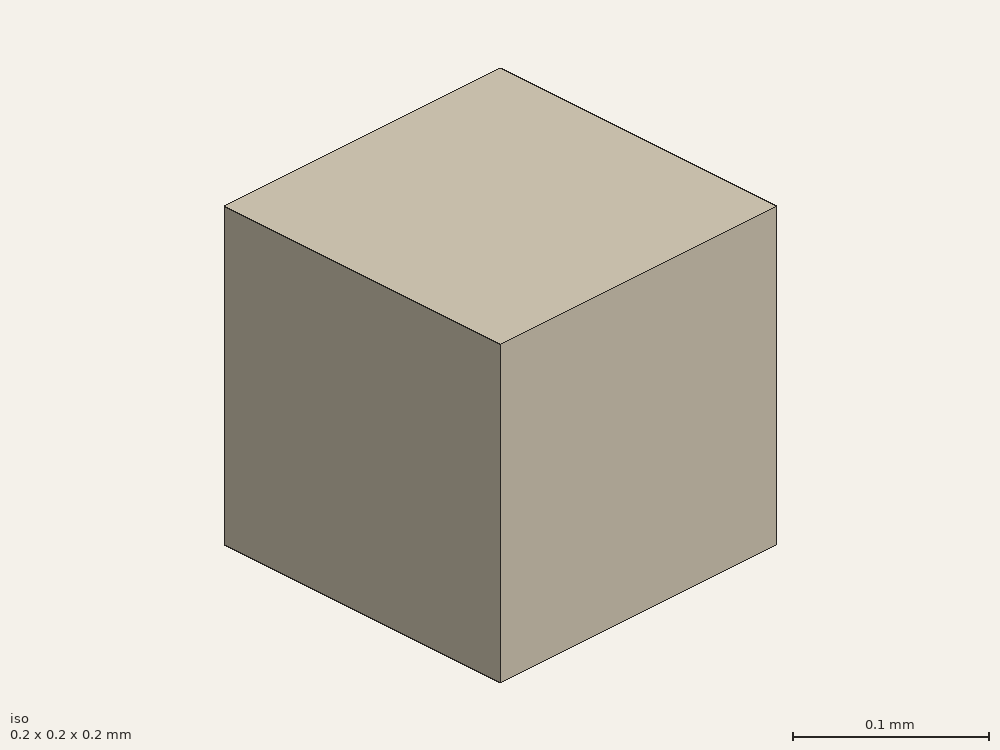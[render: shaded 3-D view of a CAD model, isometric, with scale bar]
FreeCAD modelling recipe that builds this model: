
FCSTD DOCUMENT  (FreeCAD 0.21R33694 (Git))
Label: monopole_antenna
License: All rights reserved
LicenseURL: http://en.wikipedia.org/wiki/All_rights_reserved
objects: Part::Part2DObjectPython×14, App::FeaturePython×8, Part::Extrusion×6, Part::Cut×5, Part::FeaturePython×2
note: 27 computed .brp shape members not serialized (recipe doc carries the construction recipe); baked Part::Feature solids carry a one-line shape summary decoded from their .brp

FEATURE [Part::Part2DObjectPython] Polygon  # Draft 2D object (typed FeaturePython)
  Area = 1.08e-06
  ChamferSize = 0
  DrawMode = 0
  FacesNumber = 12
  FilletRadius = 0
  MakeFace = true
  Radius = 0.0006
FEATURE [Part::Extrusion] Extrude  label="pin"
  Base = -> Polygon
  Dir = (0,0,1)
  DirMode = 2
  FaceMakerClass = Part::FaceMakerBullseye
  LengthFwd = -0.02
  LengthRev = 0
  Solid = false
  Symmetric = false
FEATURE [Part::Part2DObjectPython] Polygon001  # Draft 2D object (typed FeaturePython)
  Area = 1.28547e-05
  ChamferSize = 0
  DrawMode = 0
  FacesNumber = 12
  FilletRadius = 0
  MakeFace = true
  Radius = 0.00207
FEATURE [Part::Extrusion] Extrude001  label="dielectric"
  Base = -> Polygon001
  Dir = (0,0,1)
  DirMode = 2
  FaceMakerClass = Part::FaceMakerBullseye
  LengthFwd = -0.02
  LengthRev = 0
  Solid = false
  Symmetric = false
FEATURE [Part::Part2DObjectPython] Polygon002  # Draft 2D object (typed FeaturePython)
  Area = 1.875e-05
  ChamferSize = 0
  DrawMode = 0
  FacesNumber = 12
  FilletRadius = 0
  MakeFace = true
  Radius = 0.0025
FEATURE [Part::Extrusion] Extrude002  label="void"
  Base = -> Polygon002
  Dir = (0,0,1)
  DirMode = 2
  FaceMakerClass = Part::FaceMakerBullseye
  LengthFwd = -0.021
  LengthRev = 0
  Solid = false
  Symmetric = false
FEATURE [Part::Part2DObjectPython] Rectangle  # Draft 2D object (typed FeaturePython)
  Area = 0.01
  ChamferSize = 0
  Columns = 1
  FilletRadius = 0
  Height = 0.1
  Length = 0.1
  MakeFace = true
  Placement = pos=(-0.05,-0.05,0) rot=(0,0,1;0rad)
  Rows = 1
FEATURE [Part::Extrusion] Extrude003  label="gp"
  Base = -> Rectangle
  Dir = (0,0,1)
  DirMode = 2
  FaceMakerClass = Part::FaceMakerBullseye
  LengthFwd = -0.0005
  LengthRev = 0
  Solid = false
  Symmetric = false
FEATURE [Part::FeaturePython] Clone  label="void001"  # Draft clone (typed FeaturePython)
  AttacherType = Attacher::AttachEngine3D
  Fuse = false
  Objects = -> [Extrude002]
  Scale = (1,1,1)
FEATURE [Part::Cut] Cut  label="groundplane"
  Base = -> Extrude003
  Tool = -> Clone
FEATURE [Part::Part2DObjectPython] Polygon003  # Draft 2D object (typed FeaturePython)
  Area = 3e-06
  ChamferSize = 0
  DrawMode = 0
  FacesNumber = 12
  FilletRadius = 0
  MakeFace = true
  Radius = 0.001
FEATURE [Part::Extrusion] Extrude004  label="monopole"
  Base = -> Polygon003
  Dir = (0,0,1)
  DirMode = 2
  FaceMakerClass = Part::FaceMakerBullseye
  LengthFwd = 0.015
  LengthRev = 0
  Solid = false
  Symmetric = false
FEATURE [Part::Part2DObjectPython] Rectangle001  # Draft 2D object (typed FeaturePython)
  Area = 0.04
  ChamferSize = 0
  Columns = 1
  FilletRadius = 0
  Height = 0.2
  Length = 0.2
  MakeFace = true
  Placement = pos=(-0.1,-0.1,0) rot=(0,0,1;0rad)
  Rows = 1
FEATURE [Part::Extrusion] Extrude005  label="air"
  Base = -> Rectangle001
  Dir = (0,0,1)
  DirMode = 2
  FaceMakerClass = Part::FaceMakerBullseye
  LengthFwd = 0.2
  LengthRev = 0
  Placement = pos=(0,0,-0.1) rot=(0,0,1;0rad)
  Solid = false
  Symmetric = false
FEATURE [Part::Part2DObjectPython] Polygon004  label="_Pport"  # Draft 2D object (typed FeaturePython)
  Area = 1.28547e-05
  ChamferSize = 0
  DrawMode = 0
  FacesNumber = 12
  FilletRadius = 0
  MakeFace = true
  Placement = pos=(0,0,-0.02) rot=(0.707107,0.707107,0;3.14159rad)
  Radius = 0.00207
FEATURE [Part::Part2DObjectPython] Line  label="_Pv"  # Draft 2D object (typed FeaturePython)
  Area = 0
  ChamferSize = 0
  Closed = false
  End = (0,0.0006,-0.02)
  FilletRadius = 0
  Length = 0.00147
  MakeFace = true
  Placement = pos=(0,0.00207,-0.02) rot=(0.707107,0.707107,0;3.14159rad)
  Points = (2) [(0,0,0),(-0.00147,2.50691e-19,0)]
  Start = (0,0.00207,-0.02)
  Subdivisions = 0
FEATURE [Part::Cut] Cut001  label="teflon"
  Base = -> Extrude001
  Tool = -> Extrude
FEATURE [Part::Cut] Cut002
  Base = -> Extrude005
  Tool = -> Extrude002
FEATURE [Part::Cut] Cut003
  Base = -> Cut002
  Tool = -> Cut
FEATURE [Part::Cut] Cut004
  Base = -> Cut003
  Tool = -> Extrude004
FEATURE [Part::FeaturePython] BooleanFragments  # WARN: FeaturePython — macro-defined, semantics opaque (R4)
  Mode = 0
  Objects = -> [Cut004,Cut001]
  Tolerance = 0
FEATURE [App::FeaturePython] Text  label="_Sin(PV){port}"  # WARN: FeaturePython — macro-defined, semantics opaque (R4)
  Placement = pos=(-0.270014,-0.146224,-0.02) rot=(0.707107,0.707107,0;3.14159rad)
  Text = .
FEATURE [App::FeaturePython] Text001  label="_Min(1,voltage){v}"  # WARN: FeaturePython — macro-defined, semantics opaque (R4)
  Placement = pos=(-0.270014,-0.146224,-0.02) rot=(0.707107,0.707107,0;3.14159rad)
  Text = .
FEATURE [Part::Part2DObjectPython] Rectangle002  label="_Pfront"  # Draft 2D object (typed FeaturePython)
  Area = 0.04
  ChamferSize = 0
  Columns = 1
  FilletRadius = 0
  Height = 0.2
  Length = 0.2
  MakeFace = true
  Placement = pos=(-0.1,-0.1,-0.1) rot=(1,0,0;1.5708rad)
  Rows = 1
FEATURE [Part::Part2DObjectPython] Rectangle003  label="_Pback"  # Draft 2D object (typed FeaturePython)
  Area = 0.04
  ChamferSize = 0
  Columns = 1
  FilletRadius = 0
  Height = 0.2
  Length = 0.2
  MakeFace = true
  Placement = pos=(-0.1,0.1,-0.1) rot=(1,0,0;1.5708rad)
  Rows = 1
FEATURE [Part::Part2DObjectPython] Rectangle004  label="_Pright"  # Draft 2D object (typed FeaturePython)
  Area = 0.04
  ChamferSize = 0
  Columns = 1
  FilletRadius = 0
  Height = 0.2
  Length = 0.2
  MakeFace = true
  Placement = pos=(0.1,-0.1,-0.1) rot=(0.57735,0.57735,0.57735;2.0944rad)
  Rows = 1
FEATURE [Part::Part2DObjectPython] Rectangle005  label="_Pleft"  # Draft 2D object (typed FeaturePython)
  Area = 0.04
  ChamferSize = 0
  Columns = 1
  FilletRadius = 0
  Height = 0.2
  Length = 0.2
  MakeFace = true
  Placement = pos=(-0.1,-0.1,-0.1) rot=(0.57735,0.57735,0.57735;2.0944rad)
  Rows = 1
FEATURE [Part::Part2DObjectPython] Rectangle006  label="_Ptop"  # Draft 2D object (typed FeaturePython)
  Area = 0.04
  ChamferSize = 0
  Columns = 1
  FilletRadius = 0
  Height = 0.2
  Length = 0.2
  MakeFace = true
  Placement = pos=(-0.1,-0.1,0.1) rot=(0,0,1;0rad)
  Rows = 1
FEATURE [Part::Part2DObjectPython] Rectangle007  label="_Pbottom"  # Draft 2D object (typed FeaturePython)
  Area = 0.04
  ChamferSize = 0
  Columns = 1
  FilletRadius = 0
  Height = 0.2
  Length = 0.2
  MakeFace = true
  Placement = pos=(-0.1,-0.1,-0.1) rot=(0,0,1;0rad)
  Rows = 1
FEATURE [App::FeaturePython] Text002  label="_Bfront(radiation){front}"  # WARN: FeaturePython — macro-defined, semantics opaque (R4)
  Placement = pos=(-0.270014,-0.146224,-0.02) rot=(0.707107,0.707107,0;3.14159rad)
  Text = .
FEATURE [App::FeaturePython] Text003  label="_Bback(radiation){back}"  # WARN: FeaturePython — macro-defined, semantics opaque (R4)
  Placement = pos=(-0.270014,-0.146224,-0.02) rot=(0.707107,0.707107,0;3.14159rad)
  Text = .
FEATURE [App::FeaturePython] Text004  label="_Bleft(radiation){left}"  # WARN: FeaturePython — macro-defined, semantics opaque (R4)
  Placement = pos=(-0.270014,-0.146224,-0.02) rot=(0.707107,0.707107,0;3.14159rad)
  Text = .
FEATURE [App::FeaturePython] Text005  label="_Bright(radiation){right}"  # WARN: FeaturePython — macro-defined, semantics opaque (R4)
  Placement = pos=(-0.270014,-0.146224,-0.02) rot=(0.707107,0.707107,0;3.14159rad)
  Text = .
FEATURE [App::FeaturePython] Text006  label="_Btop(radiation){top}"  # WARN: FeaturePython — macro-defined, semantics opaque (R4)
  Placement = pos=(-0.270014,-0.146224,-0.02) rot=(0.707107,0.707107,0;3.14159rad)
  Text = .
FEATURE [App::FeaturePython] Text007  label="_Bbottom(radiation){bottom}"  # WARN: FeaturePython — macro-defined, semantics opaque (R4)
  Placement = pos=(-0.270014,-0.146224,-0.02) rot=(0.707107,0.707107,0;3.14159rad)
  Text = .
